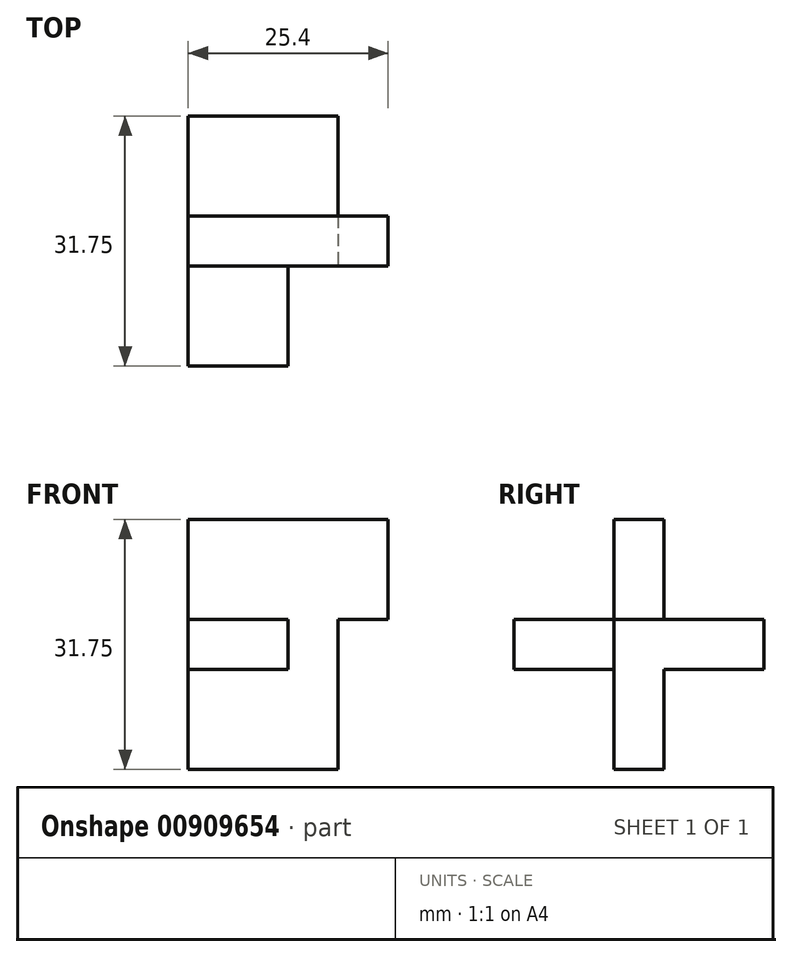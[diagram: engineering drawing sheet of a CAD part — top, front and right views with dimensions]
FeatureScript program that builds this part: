
annotation { "Feature Type Name" : "Feature", "Feature Type Description" : "" }
export const myFeature = defineFeature(function(context is Context, id is Id, definition is map)
    precondition{}
    {
        {
            var Q0;
            Q0=qCreatedBy(makeId("Right.planeOp"),FACE);
            var sketch = newSketch(context, id + "F0", { "sketchPlane" : qUnion([Q0])});
            skLineSegment(sketch, "E0.bottom", {"start": v(-8.76, 12.41) * mm, "end": v(-40.5, 12.41) * mm});
            skLineSegment(sketch, "E0.top", {"start": v(-8.76, 44.16) * mm, "end": v(-40.5, 44.16) * mm});
            skLineSegment(sketch, "E0.left", {"start": v(-8.76, 12.41) * mm, "end": v(-8.76, 44.16) * mm});
            skLineSegment(sketch, "E0.right", {"start": v(-40.5, 12.41) * mm, "end": v(-40.5, 44.16) * mm});
            skPoint(sketch, "E0.middle", {"position": v(-24.63, 28.29) * mm});
            skLineSegment(sketch, "E1.top", {"start": v(-40.5, 31.46) * mm, "end": v(-27.8, 31.46) * mm});
            skLineSegment(sketch, "E1.left", {"start": v(-40.5, 44.16) * mm, "end": v(-40.5, 31.46) * mm});
            skLineSegment(sketch, "E1.right", {"start": v(-27.8, 44.16) * mm, "end": v(-27.8, 31.46) * mm});
            skLineSegment(sketch, "E2.bottom", {"start": v(-8.76, 44.16) * mm, "end": v(-21.46, 44.16) * mm});
            skLineSegment(sketch, "E2.top", {"start": v(-8.76, 31.46) * mm, "end": v(-21.46, 31.46) * mm});
            skLineSegment(sketch, "E2.left", {"start": v(-8.76, 44.16) * mm, "end": v(-8.76, 31.46) * mm});
            skLineSegment(sketch, "E2.right", {"start": v(-21.46, 44.16) * mm, "end": v(-21.46, 31.46) * mm});
            skLineSegment(sketch, "E3.bottom", {"start": v(-8.76, 12.41) * mm, "end": v(-21.46, 12.41) * mm});
            skLineSegment(sketch, "E3.top", {"start": v(-8.76, 25.11) * mm, "end": v(-21.46, 25.11) * mm});
            skLineSegment(sketch, "E3.left", {"start": v(-8.76, 12.41) * mm, "end": v(-8.76, 25.11) * mm});
            skLineSegment(sketch, "E3.right", {"start": v(-21.46, 12.41) * mm, "end": v(-21.46, 25.11) * mm});
            skLineSegment(sketch, "E4.bottom", {"start": v(-40.5, 12.41) * mm, "end": v(-27.8, 12.41) * mm});
            skLineSegment(sketch, "E4.top", {"start": v(-40.5, 25.11) * mm, "end": v(-27.8, 25.11) * mm});
            skLineSegment(sketch, "E4.left", {"start": v(-40.5, 12.41) * mm, "end": v(-40.5, 25.11) * mm});
            skLineSegment(sketch, "E4.right", {"start": v(-27.8, 12.41) * mm, "end": v(-27.8, 25.11) * mm});
            skLineSegment(sketch, "E5", {"start": v(-21.46, 31.46) * mm, "end": v(-27.8, 31.46) * mm});
            skSolve(sketch);
        }
        {
            var Q0;
            {var subQ0=sQuery(id+"F0.wireOp",EDGE,"E1.top");Q0=makeQuery(id+"F0.imprint","IMPRINT",FACE,{"disambiguationData":[TD([[makeQuery(id+"F0.imprint","IMPRINT",EDGE,{"derivedFrom":subQ0}),-1.0]])]});}
            var Q1;
            {var subQ0=sQuery(id+"F0.wireOp",EDGE,"E1.right");Q1=makeQuery(id+"F0.imprint","IMPRINT",FACE,{"disambiguationData":[TD([[makeQuery(id+"F0.imprint","IMPRINT",EDGE,{"derivedFrom":subQ0}),1.0]])]});}
            extrude(context, id + "F1", {"entities" : qUnion([Q0, Q1]), "depth" : 19.05 * mm, "offsetDistance" : 25.4 * mm});
        }
        {
            var Q0;
            Q0=makeQuery(id+"F1.opExtrude","CAP_FACE",FACE,{"disambiguationData":[OSD([sQuery(id+"F0.wireOp",EDGE,"E0.bottom"),sQuery(id+"F0.wireOp",EDGE,"E0.top"),sQuery(id+"F0.wireOp",EDGE,"E0.left"),sQuery(id+"F0.wireOp",EDGE,"E0.right"),sQuery(id+"F0.wireOp",EDGE,"E1.top"),sQuery(id+"F0.wireOp",EDGE,"E1.right"),sQuery(id+"F0.wireOp",EDGE,"E2.top"),sQuery(id+"F0.wireOp",EDGE,"E2.right"),sQuery(id+"F0.wireOp",EDGE,"E3.top"),sQuery(id+"F0.wireOp",EDGE,"E3.right"),sQuery(id+"F0.wireOp",EDGE,"E4.top"),sQuery(id+"F0.wireOp",EDGE,"E4.right")])],"isStart":false});
            var sketch = newSketch(context, id + "F2", { "sketchPlane" : qUnion([Q0])});
            skLineSegment(sketch, "E6", {"start": v(-21.46, 31.46) * mm, "end": v(-27.8, 31.46) * mm});
            skSolve(sketch);
        }
        {
            var Q0;
            Q0=makeQuery(id+"F2.imprint","IMPRINT",FACE,{"disambiguationData":[TD([[makeQuery(id+"F2.imprint","IMPRINT",EDGE,{"derivedFrom":sQuery(id+"F2.wireOp",EDGE,"E6")}),-1.0]])]});
            extrude(context, id + "F3", {"entities" : qUnion([Q0]), "operationType" : NewBodyOperationType.ADD, "depth" : 6.35 * mm, "offsetDistance" : 25.4 * mm});
        }
        {
            var Q0;
            Q0=makeQuery(id+"F1.opExtrude","CAP_FACE",FACE,{"disambiguationData":[OSD([sQuery(id+"F0.wireOp",EDGE,"E0.bottom"),sQuery(id+"F0.wireOp",EDGE,"E0.top"),sQuery(id+"F0.wireOp",EDGE,"E0.left"),sQuery(id+"F0.wireOp",EDGE,"E0.right"),sQuery(id+"F0.wireOp",EDGE,"E1.top"),sQuery(id+"F0.wireOp",EDGE,"E1.right"),sQuery(id+"F0.wireOp",EDGE,"E2.top"),sQuery(id+"F0.wireOp",EDGE,"E2.right"),sQuery(id+"F0.wireOp",EDGE,"E3.top"),sQuery(id+"F0.wireOp",EDGE,"E3.right"),sQuery(id+"F0.wireOp",EDGE,"E4.top"),sQuery(id+"F0.wireOp",EDGE,"E4.right")])],"isStart":false});
            var sketch = newSketch(context, id + "F4", { "sketchPlane" : qUnion([Q0])});
            skLineSegment(sketch, "E7", {"start": v(-27.8, 31.46) * mm, "end": v(-27.8, 25.11) * mm});
            skSolve(sketch);
        }
        {
            var Q0;
            Q0=makeQuery(id+"F4.imprint","IMPRINT",FACE,{"disambiguationData":[TD([[makeQuery(id+"F4.imprint","IMPRINT",EDGE,{"derivedFrom":sQuery(id+"F4.wireOp",EDGE,"E7")}),-1.0]])]});
            extrude(context, id + "F5", {"entities" : qUnion([Q0]), "operationType" : NewBodyOperationType.REMOVE, "oppositeDirection" : true, "depth" : 6.35 * mm, "offsetDistance" : 25.4 * mm});
        }
    });
